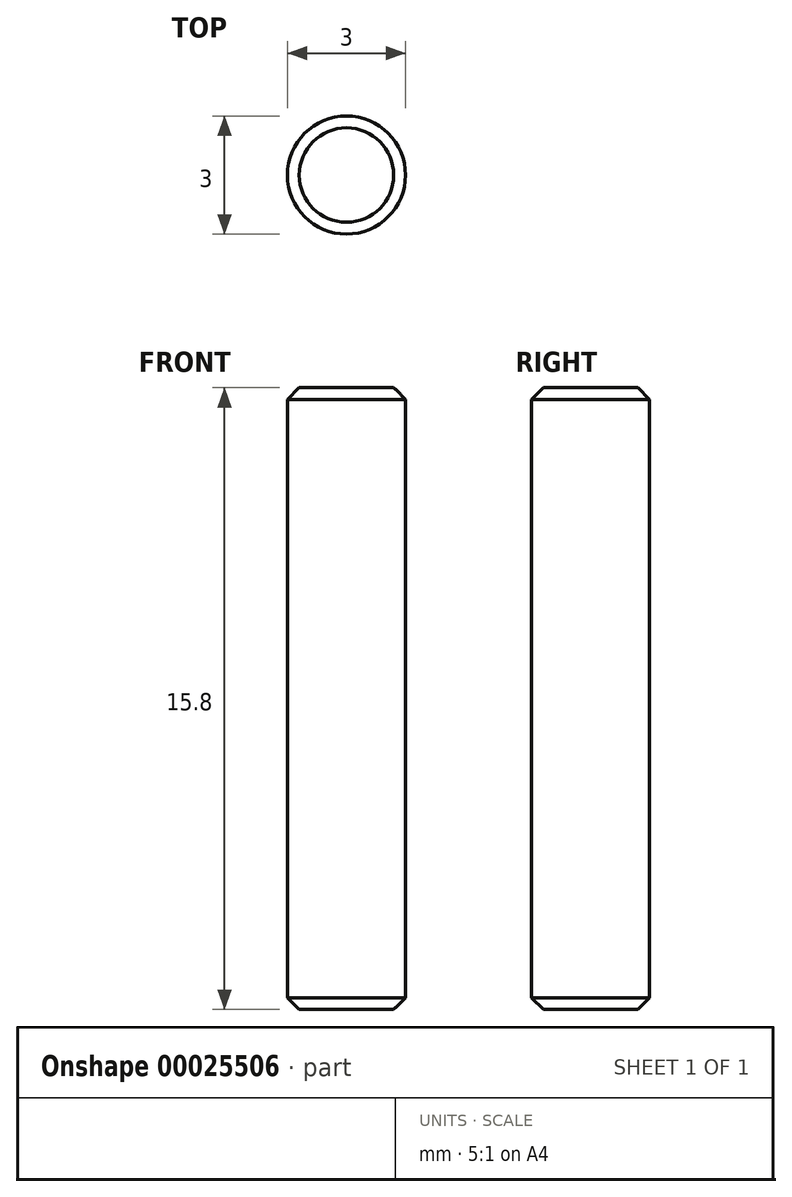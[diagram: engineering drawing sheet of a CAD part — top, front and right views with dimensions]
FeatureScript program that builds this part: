
annotation { "Feature Type Name" : "Feature", "Feature Type Description" : "" }
export const myFeature = defineFeature(function(context is Context, id is Id, definition is map)
    precondition{}
    {
        {
            var Q0;
            Q0=qCreatedBy(makeId("Top.planeOp"),FACE);
            var sketch = newSketch(context, id + "F0", { "sketchPlane" : qUnion([Q0])});
            skCircle(sketch, "E0", {"center": v(0, 0) * mm, "radius": 1.5 * mm});
            skSolve(sketch);
        }
        {
            var Q0;
            Q0 = qSketchRegion(id + "F0", true);
            extrude(context, id + "F1", {"entities" : qUnion([Q0]), "depth" : 15.8 * mm});
        }
        {
            var Q0;
            Q0=makeQuery(id+"F1.opExtrude","CAP_EDGE",EDGE,{"disambiguationData":[OSD([sQuery(id+"F0.wireOp",EDGE,"E0")])],"isStart":false});
            var Q1;
            Q1=makeQuery(id+"F1.opExtrude","CAP_EDGE",EDGE,{"disambiguationData":[OSD([sQuery(id+"F0.wireOp",EDGE,"E0")])],"isStart":true});
            chamfer(context, id + "F2", {"entities" : qUnion([Q0, Q1]), "width" : .3 * mm, "tangentPropagation" : true});
        }
    });
